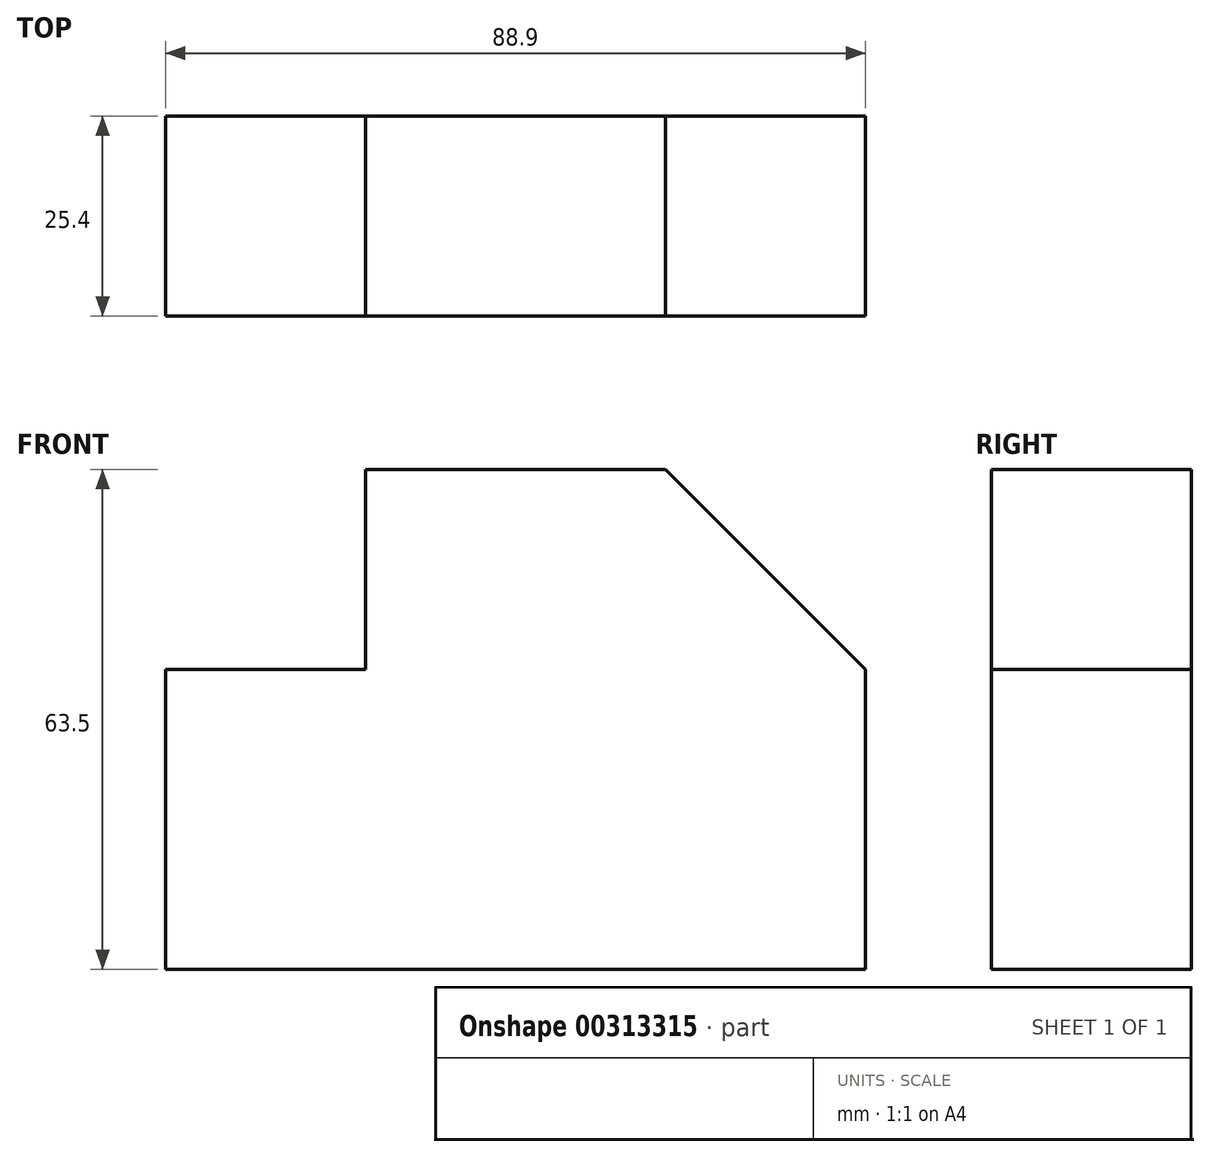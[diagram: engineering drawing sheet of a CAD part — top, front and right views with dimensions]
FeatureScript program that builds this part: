
annotation { "Feature Type Name" : "Feature", "Feature Type Description" : "" }
export const myFeature = defineFeature(function(context is Context, id is Id, definition is map)
    precondition{}
    {
        {
            var Q0;
            Q0=qCreatedBy(makeId("Front.planeOp"),FACE);
            var sketch = newSketch(context, id + "F0", { "sketchPlane" : qUnion([Q0])});
            skLineSegment(sketch, "E0", {"start": v(-44.76, -31.42) * mm, "end": v(44.14, -31.42) * mm});
            skLineSegment(sketch, "E1", {"start": v(-44.76, -31.42) * mm, "end": v(-44.76, 6.68) * mm});
            skLineSegment(sketch, "E2", {"start": v(-44.76, 6.68) * mm, "end": v(-19.36, 6.68) * mm});
            skLineSegment(sketch, "E3", {"start": v(-19.36, 6.68) * mm, "end": v(-19.36, 32.08) * mm});
            skLineSegment(sketch, "E4", {"start": v(-19.36, 32.08) * mm, "end": v(18.74, 32.08) * mm});
            skLineSegment(sketch, "E5", {"start": v(44.14, -31.42) * mm, "end": v(44.14, 6.68) * mm});
            skLineSegment(sketch, "E6", {"start": v(44.14, 6.68) * mm, "end": v(18.74, 32.08) * mm});
            skSolve(sketch);
        }
        {
            var Q0;
            Q0=makeQuery(id+"F0.imprint","IMPRINT",FACE,{"disambiguationData":[TD([[makeQuery(id+"F0.imprint","IMPRINT",EDGE,{"derivedFrom":sQuery(id+"F0.wireOp",EDGE,"E0")}),1.0]])]});
            extrude(context, id + "F1", {"entities" : qUnion([Q0]), "depth" : 25.4 * mm});
        }
    });
